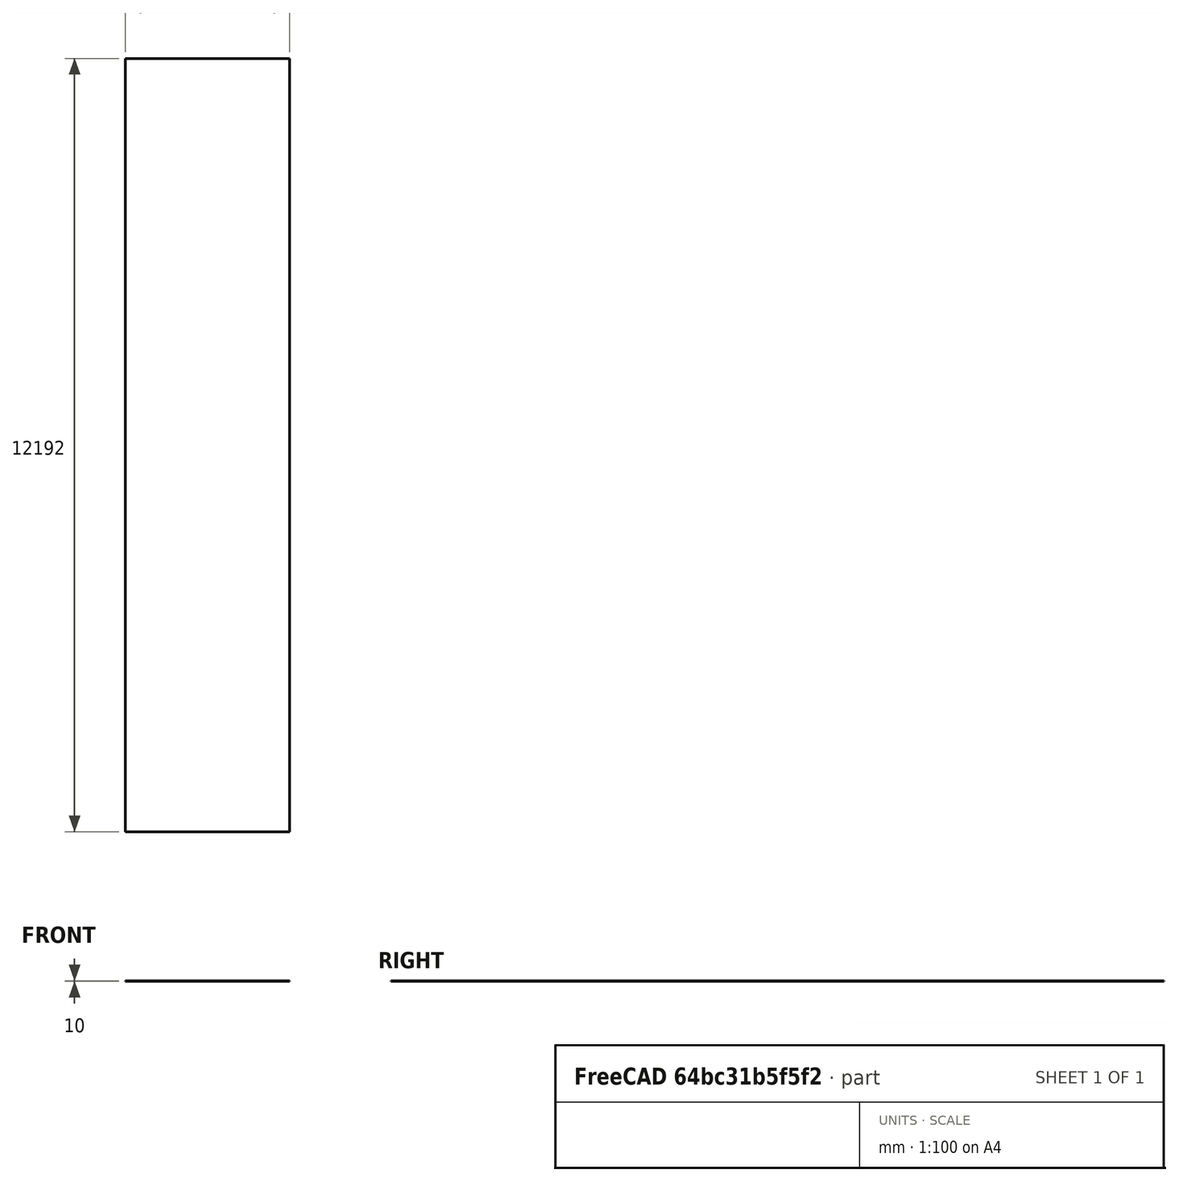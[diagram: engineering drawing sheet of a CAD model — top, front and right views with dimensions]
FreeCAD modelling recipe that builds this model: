
FCSTD DOCUMENT  (FreeCAD 2023.131R26244 +5365 (Git))
Label: roadLegalWidth
License: All rights reserved
LicenseURL: http://en.wikipedia.org/wiki/All_rights_reserved
objects: Sketcher::SketchObject×1, PartDesign::Pad×1, PartDesign::Body×1, App::Part×1
note: 6 computed .brp shape members not serialized (recipe doc carries the construction recipe); baked Part::Feature solids carry a one-line shape summary decoded from their .brp

FEATURE [Sketcher::SketchObject] Sketch
  ArcFitTolerance = 1e-06
  AttachmentSupport = -> [XY_Plane]
  ExternalBSplineMaxDegree = 5
  ExternalBSplineTolerance = 0.0001
  FullyConstrained = true
  InternalTolerance = 1e-06
  InvalidShape = false
  MakeInternals = false
  MapMode = 5
  Support = -> [XY_Plane]
  TreeRank = 10
  ValidateShape = true
  sketch-geometry (4):
    g0: LineSegment StartX=0 StartY=0 StartZ=0 EndX=2590.8 EndY=0 EndZ=0
    g1: LineSegment StartX=2590.8 StartY=0 StartZ=0 EndX=2590.8 EndY=12192 EndZ=0
    g2: LineSegment StartX=2590.8 StartY=12192 StartZ=0 EndX=0 EndY=12192 EndZ=0
    g3: LineSegment StartX=0 StartY=12192 StartZ=0 EndX=0 EndY=0 EndZ=0
  constraints (11):
    c: Coincident(g0,g1)
    c: Coincident(g1,g2)
    c: Coincident(g2,g3)
    c: Coincident(g3,g0)
    c: Horizontal(g0)
    c: Horizontal(g2)
    c: Vertical(g1)
    c: Vertical(g3)
    c: Coincident(g0,g-1)
    c: DistanceX(g0,g0) = 2590.8
    c: DistanceY(g3,g3) = 12192
FEATURE [PartDesign::Pad] Pad
  AddSubType = 0
  AlongSketchNormal = false
  AutoTaperInnerAngle = true
  CheckUpToFaceLimits = true
  ClaimChildren = false
  Direction = (0,0,1)
  Fit = 0
  FitJoin = 0
  FixShape = 1
  InnerFit = 0
  InnerFitJoin = 0
  InvalidShape = false
  Length = 10
  Length2 = 100
  Linearize = true
  NewSolid = false
  Profile = -> Sketch
  Reversed = true
  Suppress = false
  TaperInnerAngle = 0
  TaperInnerAngleRev = 0
  TreeRank = 11
  Type = 0
  ValidateShape = false
  _ProfileBasedVersion = 1
FEATURE [PartDesign::Body] Body  label="roadLegalWidth-Body"
  AutoGroupSolids = false
  ClaimAllChildren = false
  ExportMode = 0
  Group = -> [Sketch,Pad]
  InvalidShape = false
  Origin = -> Origin
  Tip = -> Pad
  TreeRank = 9
  ValidateShape = true
  _ExportChildren = -> [Pad]
  _GroupVersion = 1
FEATURE [App::Part] Part  label="roadLegalWidth-Part"
  ClaimAllChildren = false
  ExportMode = 1
  Group = -> [Body]
  Origin = -> Origin001
  TreeRank = 14
  _ExportChildren = -> [Body]
  _GroupVersion = 1
